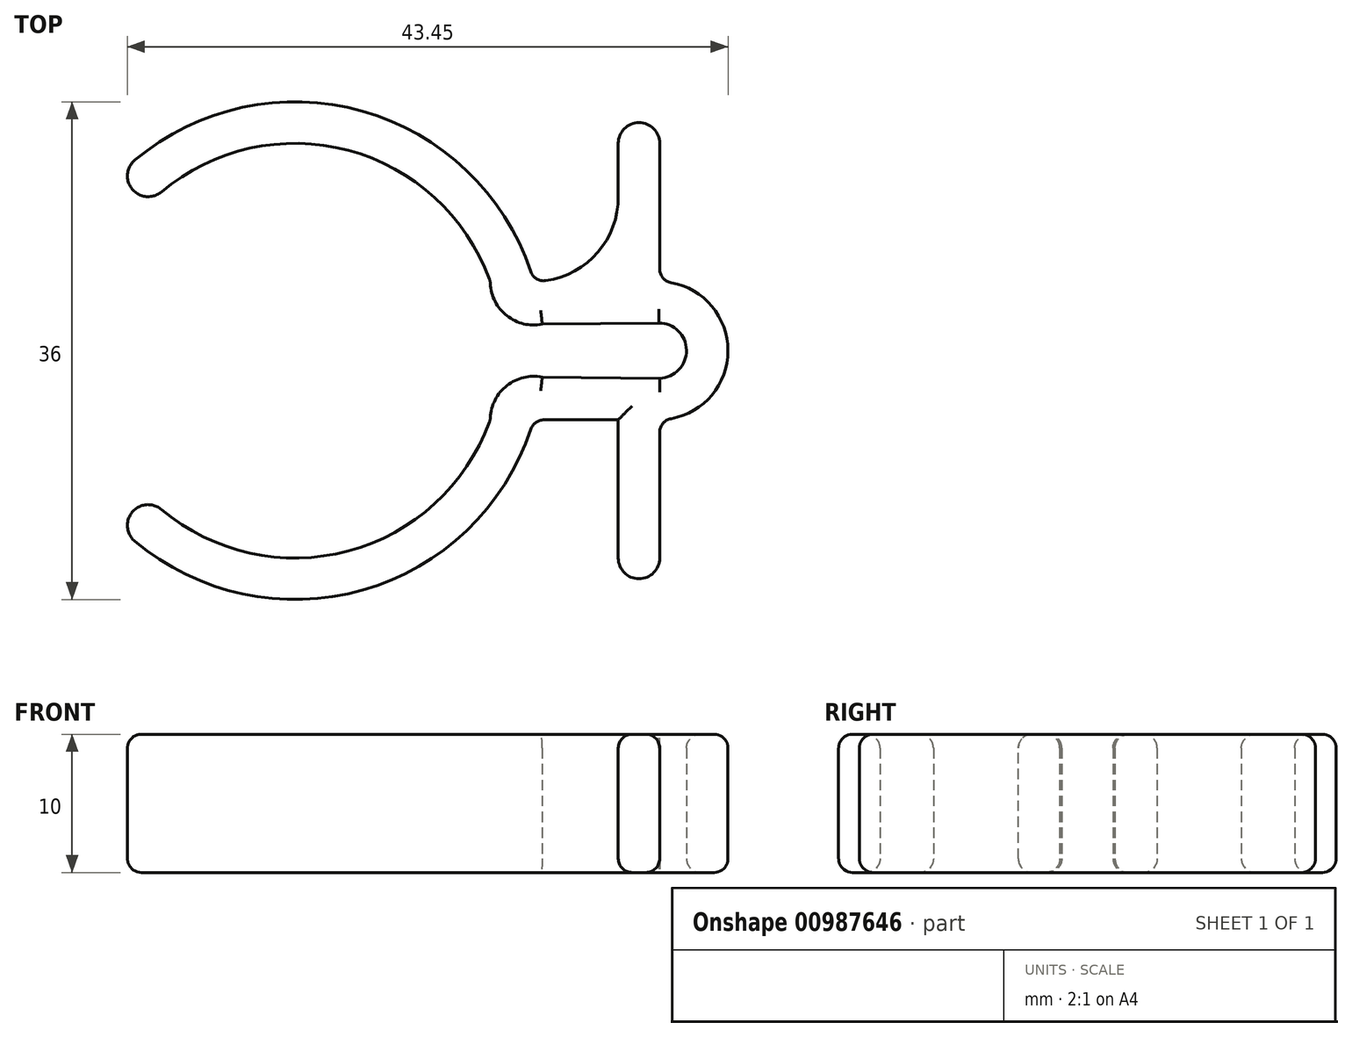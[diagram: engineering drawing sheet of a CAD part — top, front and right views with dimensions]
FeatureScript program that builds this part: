
annotation { "Feature Type Name" : "Feature", "Feature Type Description" : "" }
export const myFeature = defineFeature(function(context is Context, id is Id, definition is map)
    precondition{}
    {
        {
            var Q0;
            Q0=qCreatedBy(makeId("Top.planeOp"),FACE);
            var sketch = newSketch(context, id + "F0", { "sketchPlane" : qUnion([Q0])});
            skArc(sketch, "E0", {"start": v(14.14, 5) * mm, "mid": v(3.95, 14.47) * mm, "end": v(-9.64, 11.5) * mm});
            skArc(sketch, "E1.0", {"start": v(17.3, 5) * mm, "mid": v(5.24, 17.22) * mm, "end": v(-11.57, 13.79) * mm});
            skLineSegment(sketch, "E2", {"start": v(0, 0) * mm, "end": v(-9.64, 11.5) * mm, "construction": true});
            skLineSegment(sketch, "E3", {"start": v(0, 0) * mm, "end": v(-9.64, -11.5) * mm, "construction": true});
            skLineSegment(sketch, "E4", {"start": v(0, 0) * mm, "end": v(37.21, 0) * mm, "construction": true});
            skLineSegment(sketch, "E5", {"start": v(26.4, 5) * mm, "end": v(17.3, 5) * mm});
            skArc(sketch, "E6", {"start": v(26.4, -5) * mm, "mid": v(31.34, 0) * mm, "end": v(26.4, 5) * mm});
            skArc(sketch, "E7", {"start": v(26.34, 2) * mm, "mid": v(28.34, 0.03) * mm, "end": v(26.4, -2) * mm});
            skArc(sketch, "E8", {"start": v(14.14, 5) * mm, "mid": v(15.3, 2.57) * mm, "end": v(17.9, 1.9) * mm});
            skArc(sketch, "E9", {"start": v(14.14, -5) * mm, "mid": v(15.3, -2.57) * mm, "end": v(17.9, -1.9) * mm});
            skLineSegment(sketch, "E10", {"start": v(17.9, 1.9) * mm, "end": v(26.34, 2) * mm});
            skLineSegment(sketch, "E11", {"start": v(26.4, -2) * mm, "end": v(17.9, -1.9) * mm});
            skLineSegment(sketch, "E12.trimOffspring", {"start": v(17.3, -5) * mm, "end": v(26.4, -5) * mm});
            skArc(sketch, "E13.trimOffspring", {"start": v(-9.64, -11.5) * mm, "mid": v(3.95, -14.47) * mm, "end": v(14.14, -5) * mm});
            skArc(sketch, "E14.trimOffspring", {"start": v(-11.57, -13.79) * mm, "mid": v(5.24, -17.22) * mm, "end": v(17.3, -5) * mm});
            skLineSegment(sketch, "E15", {"start": v(-9.64, 11.5) * mm, "end": v(-11.57, 13.79) * mm});
            skLineSegment(sketch, "E16", {"start": v(-9.64, -11.5) * mm, "end": v(-11.57, -13.79) * mm});
            skArc(sketch, "E17", {"start": v(-11.57, 13.79) * mm, "mid": v(-11.76, 11.68) * mm, "end": v(-9.64, 11.5) * mm});
            skArc(sketch, "E18", {"start": v(-9.64, -11.5) * mm, "mid": v(-11.76, -11.68) * mm, "end": v(-11.57, -13.79) * mm});
            skLineSegment(sketch, "E19", {"start": v(26.4, 5) * mm, "end": v(26.4, 15) * mm});
            skLineSegment(sketch, "E20", {"start": v(26.4, -5) * mm, "end": v(26.4, -15) * mm});
            skLineSegment(sketch, "E21.0", {"start": v(23.4, -5) * mm, "end": v(23.4, -20) * mm});
            skLineSegment(sketch, "E22.0", {"start": v(23.4, 5) * mm, "end": v(23.4, 20) * mm});
            skLineSegment(sketch, "E23", {"start": v(17.3, 5) * mm, "end": v(17.3, 11.1) * mm});
            skLineSegment(sketch, "E24", {"start": v(17.3, -5) * mm, "end": v(17.3, -11.1) * mm});
            skArc(sketch, "E25", {"start": v(17.3, -5) * mm, "mid": v(21.6, -6.77) * mm, "end": v(23.4, -11.06) * mm});
            skArc(sketch, "E26", {"start": v(17.3, 5) * mm, "mid": v(21.63, 6.8) * mm, "end": v(23.4, 11.16) * mm});
            skLineSegment(sketch, "E27", {"start": v(26.4, 15) * mm, "end": v(23.4, 15) * mm});
            skLineSegment(sketch, "E28", {"start": v(26.4, -15) * mm, "end": v(23.4, -15) * mm});
            skArc(sketch, "E29", {"start": v(23.4, 15) * mm, "mid": v(24.9, 16.5) * mm, "end": v(26.4, 15) * mm});
            skArc(sketch, "E30", {"start": v(23.4, -15) * mm, "mid": v(24.9, -16.5) * mm, "end": v(26.4, -15) * mm});
            skSolve(sketch);
        }
        {
            var Q0;
            Q0=makeQuery(id+"F0.imprint","IMPRINT",FACE,{"disambiguationData":[TD([[makeQuery(id+"F0.imprint","IMPRINT",EDGE,{"derivedFrom":sQuery(id+"F0.wireOp",EDGE,"E0")}),-1.0]])]});
            var Q1;
            Q1=makeQuery(id+"F0.imprint","IMPRINT",FACE,{"disambiguationData":[TD([[makeQuery(id+"F0.imprint","IMPRINT",EDGE,{"derivedFrom":sQuery(id+"F0.wireOp",EDGE,"E15")}),1.0]])]});
            var Q2;
            Q2=makeQuery(id+"F0.imprint","IMPRINT",FACE,{"disambiguationData":[TD([[makeQuery(id+"F0.imprint","IMPRINT",EDGE,{"derivedFrom":sQuery(id+"F0.wireOp",EDGE,"E16")}),-1.0]])]});
            var Q3;
            {var subQ1=sQuery(id+"F0.wireOp",EDGE,"E5");var subQ3=sQuery(id+"F0.wireOp",EDGE,"E22.0");var subQ4=makeQuery(id+"F0.imprint","INTERSECT",VERTEX,{"derivedFrom":[subQ1,subQ3]});Q3=makeQuery(id+"F0.imprint","IMPRINT",FACE,{"disambiguationData":[TD([[makeQuery(id+"F0.imprint","IMPRINT",EDGE,{"disambiguationData":[TD([[subQ4,-1.0]])],"derivedFrom":subQ3}),1.0]])]});}
            var Q4;
            {var subQ4=sQuery(id+"F0.wireOp",EDGE,"E19");Q4=makeQuery(id+"F0.imprint","IMPRINT",FACE,{"disambiguationData":[TD([[makeQuery(id+"F0.imprint","IMPRINT",EDGE,{"derivedFrom":subQ4}),1.0]])]});}
            var Q5;
            {var subQ4=sQuery(id+"F0.wireOp",EDGE,"E20");Q5=makeQuery(id+"F0.imprint","IMPRINT",FACE,{"disambiguationData":[TD([[makeQuery(id+"F0.imprint","IMPRINT",EDGE,{"derivedFrom":subQ4}),-1.0]])]});}
            var Q6;
            {var subQ0=sQuery(id+"F0.wireOp",EDGE,"E25");Q6=makeQuery(id+"F0.imprint","IMPRINT",FACE,{"disambiguationData":[TD([[makeQuery(id+"F0.imprint","IMPRINT",EDGE,{"derivedFrom":subQ0}),1.0]])]});}
            var Q7;
            Q7=makeQuery(id+"F0.imprint","IMPRINT",FACE,{"disambiguationData":[TD([[makeQuery(id+"F0.imprint","IMPRINT",EDGE,{"derivedFrom":sQuery(id+"F0.wireOp",EDGE,"E28")}),1.0]])]});
            var Q8;
            Q8=makeQuery(id+"F0.imprint","IMPRINT",FACE,{"disambiguationData":[TD([[makeQuery(id+"F0.imprint","IMPRINT",EDGE,{"derivedFrom":sQuery(id+"F0.wireOp",EDGE,"E27")}),-1.0]])]});
            extrude(context, id + "F1", {"entities" : qUnion([Q0, Q1, Q2, Q3, Q4, Q5, Q6, Q7, Q8]), "depth" : 10 * mm, "offsetDistance" : 25 * mm});
        }
        {
            var Q0;
            Q0=makeQuery(id+"F1.opExtrude","CAP_FACE",FACE,{"disambiguationData":[OSD([sQuery(id+"F0.wireOp",EDGE,"E0"),sQuery(id+"F0.wireOp",EDGE,"E1.0"),sQuery(id+"F0.wireOp",EDGE,"E6"),sQuery(id+"F0.wireOp",EDGE,"E7"),sQuery(id+"F0.wireOp",EDGE,"E8"),sQuery(id+"F0.wireOp",EDGE,"E9"),sQuery(id+"F0.wireOp",EDGE,"E10"),sQuery(id+"F0.wireOp",EDGE,"E11"),sQuery(id+"F0.wireOp",EDGE,"E13.trimOffspring"),sQuery(id+"F0.wireOp",EDGE,"E14.trimOffspring"),sQuery(id+"F0.wireOp",EDGE,"E17"),sQuery(id+"F0.wireOp",EDGE,"E18"),sQuery(id+"F0.wireOp",EDGE,"E19"),sQuery(id+"F0.wireOp",EDGE,"E20"),sQuery(id+"F0.wireOp",EDGE,"E21.0"),sQuery(id+"F0.wireOp",EDGE,"E22.0"),sQuery(id+"F0.wireOp",EDGE,"E25"),sQuery(id+"F0.wireOp",EDGE,"E26"),sQuery(id+"F0.wireOp",EDGE,"E29"),sQuery(id+"F0.wireOp",EDGE,"E30")])],"isStart":false});
            var Q1;
            Q1=makeQuery(id+"F1.opExtrude","CAP_FACE",FACE,{"disambiguationData":[OSD([sQuery(id+"F0.wireOp",EDGE,"E0"),sQuery(id+"F0.wireOp",EDGE,"E1.0"),sQuery(id+"F0.wireOp",EDGE,"E6"),sQuery(id+"F0.wireOp",EDGE,"E7"),sQuery(id+"F0.wireOp",EDGE,"E8"),sQuery(id+"F0.wireOp",EDGE,"E9"),sQuery(id+"F0.wireOp",EDGE,"E10"),sQuery(id+"F0.wireOp",EDGE,"E11"),sQuery(id+"F0.wireOp",EDGE,"E13.trimOffspring"),sQuery(id+"F0.wireOp",EDGE,"E14.trimOffspring"),sQuery(id+"F0.wireOp",EDGE,"E17"),sQuery(id+"F0.wireOp",EDGE,"E18"),sQuery(id+"F0.wireOp",EDGE,"E19"),sQuery(id+"F0.wireOp",EDGE,"E20"),sQuery(id+"F0.wireOp",EDGE,"E21.0"),sQuery(id+"F0.wireOp",EDGE,"E22.0"),sQuery(id+"F0.wireOp",EDGE,"E25"),sQuery(id+"F0.wireOp",EDGE,"E26"),sQuery(id+"F0.wireOp",EDGE,"E29"),sQuery(id+"F0.wireOp",EDGE,"E30")])],"isStart":true});
            var Q2;
            Q2=makeQuery(id+"F1.opExtrude","SWEPT_EDGE",EDGE,{"disambiguationData":[OSD([sQuery(id+"F0.wireOp",EDGE,"E5"),sQuery(id+"F0.wireOp",EDGE,"E6"),sQuery(id+"F0.wireOp",EDGE,"E19")])]});
            var Q3;
            Q3=makeQuery(id+"F1.opExtrude","SWEPT_EDGE",EDGE,{"disambiguationData":[OSD([sQuery(id+"F0.wireOp",EDGE,"E6"),sQuery(id+"F0.wireOp",EDGE,"E12.trimOffspring"),sQuery(id+"F0.wireOp",EDGE,"E20")])]});
            var Q4;
            Q4=makeQuery(id+"F1.opExtrude","SWEPT_EDGE",EDGE,{"disambiguationData":[OSD([sQuery(id+"F0.wireOp",EDGE,"E12.trimOffspring"),sQuery(id+"F0.wireOp",EDGE,"E14.trimOffspring"),sQuery(id+"F0.wireOp",EDGE,"E25")])]});
            var Q5;
            Q5=makeQuery(id+"F1.opExtrude","SWEPT_EDGE",EDGE,{"disambiguationData":[OSD([sQuery(id+"F0.wireOp",EDGE,"E1.0"),sQuery(id+"F0.wireOp",EDGE,"E5"),sQuery(id+"F0.wireOp",EDGE,"E26")])]});
            var Q6;
            Q6=makeQuery(id+"F1.opExtrude","SWEPT_EDGE",EDGE,{"disambiguationData":[OSD([sQuery(id+"F0.wireOp",EDGE,"E0"),sQuery(id+"F0.wireOp",EDGE,"E8")])]});
            var Q7;
            Q7=makeQuery(id+"F1.opExtrude","SWEPT_EDGE",EDGE,{"disambiguationData":[OSD([sQuery(id+"F0.wireOp",EDGE,"E9"),sQuery(id+"F0.wireOp",EDGE,"E13.trimOffspring")])]});
            fillet(context, id + "F2", {"entities" : qUnion([Q0, Q1, Q2, Q3, Q4, Q5, Q6, Q7]), "radius" : 1 * mm, "tangentPropagation" : true, "allowEdgeOverflow" : false});
        }
    });
